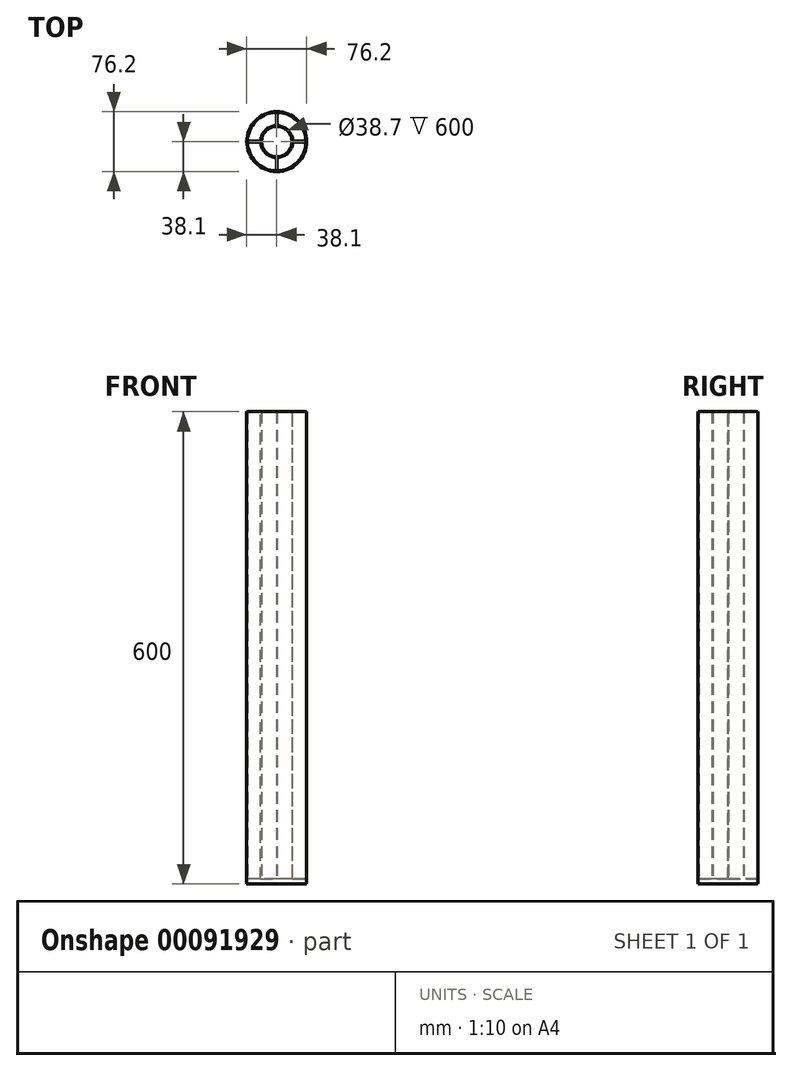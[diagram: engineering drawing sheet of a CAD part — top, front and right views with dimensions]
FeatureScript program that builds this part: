
annotation { "Feature Type Name" : "Feature", "Feature Type Description" : "" }
export const myFeature = defineFeature(function(context is Context, id is Id, definition is map)
    precondition{}
    {
        {
            var Q0;
            Q0=qCreatedBy(makeId("Top.planeOp"),FACE);
            var sketch = newSketch(context, id + "F0", { "sketchPlane" : qUnion([Q0])});
            skCircle(sketch, "E0", {"center": v(0, 0) * mm, "radius": 19.35 * mm});
            skCircle(sketch, "E1", {"center": v(0, 0) * mm, "radius": 38.1 * mm});
            skCircle(sketch, "E2.0", {"center": v(0, 0) * mm, "radius": 37.1 * mm});
            skCircle(sketch, "E3.0", {"center": v(0, 0) * mm, "radius": 20.35 * mm});
            skLineSegment(sketch, "E4.left", {"start": v(-20.35, 0) * mm, "end": v(-20.35, 0) * mm});
            skLineSegment(sketch, "E4.right", {"start": v(-37.1, 0) * mm, "end": v(-37.1, 0) * mm});
            skLineSegment(sketch, "E5.0", {"start": v(-20.35, 0.5) * mm, "end": v(-37, 0.5) * mm});
            skLineSegment(sketch, "E6.0", {"start": v(-20.35, -0.5) * mm, "end": v(-37, -0.5) * mm});
            skLineSegment(sketch, "E7.0", {"start": v(-0.5, 37.27) * mm, "end": v(-0.5, 20.35) * mm});
            skLineSegment(sketch, "E8.0", {"start": v(0.5, 37.27) * mm, "end": v(0.5, 20.35) * mm});
            skLineSegment(sketch, "E9.0", {"start": v(20.35, -0.5) * mm, "end": v(37.64, -0.5) * mm});
            skLineSegment(sketch, "E10.0", {"start": v(20.35, 0.5) * mm, "end": v(37.64, 0.5) * mm});
            skLineSegment(sketch, "E11", {"start": v(20.35, 0.5) * mm, "end": v(20.35, -0.5) * mm});
            skLineSegment(sketch, "E12", {"start": v(37.64, -0.5) * mm, "end": v(37.64, 0.5) * mm});
            skLineSegment(sketch, "E13", {"start": v(-0.5, 20.35) * mm, "end": v(0.5, 20.35) * mm});
            skLineSegment(sketch, "E14", {"start": v(-0.5, 37.27) * mm, "end": v(0.5, 37.27) * mm});
            skLineSegment(sketch, "E15", {"start": v(-37, 0.5) * mm, "end": v(-37, -0.5) * mm});
            skLineSegment(sketch, "E16", {"start": v(-20.35, 0.5) * mm, "end": v(-20.35, -0.5) * mm});
            skLineSegment(sketch, "E17.0", {"start": v(-0.5, -20.35) * mm, "end": v(-0.5, -37.2) * mm});
            skLineSegment(sketch, "E18.0", {"start": v(0.5, -20.35) * mm, "end": v(0.5, -37.2) * mm});
            skLineSegment(sketch, "E19", {"start": v(-0.5, -37.2) * mm, "end": v(0.5, -37.2) * mm});
            skLineSegment(sketch, "E20", {"start": v(0.5, -20.35) * mm, "end": v(-0.5, -20.35) * mm});
            skSolve(sketch);
        }
        {
            var Q0;
            {var subQ3=sQuery(id+"F0.wireOp",EDGE,"E2.0");var subQ5=sQuery(id+"F0.wireOp",EDGE,"E10.0");var subQ6=makeQuery(id+"F0.imprint","INTERSECT",VERTEX,{"derivedFrom":[subQ3,subQ5]});Q0=makeQuery(id+"F0.imprint","IMPRINT",FACE,{"disambiguationData":[TD([[makeQuery(id+"F0.imprint","IMPRINT",EDGE,{"disambiguationData":[TD([[subQ6,1.0]])],"derivedFrom":subQ3}),1.0]])]});}
            var Q1;
            {var subQ5=sQuery(id+"F0.wireOp",EDGE,"E12");Q1=makeQuery(id+"F0.imprint","IMPRINT",FACE,{"disambiguationData":[TD([[makeQuery(id+"F0.imprint","IMPRINT",EDGE,{"derivedFrom":subQ5}),1.0]])]});}
            var Q2;
            Q2=makeQuery(id+"F0.imprint","IMPRINT",FACE,{"disambiguationData":[TD([[makeQuery(id+"F0.imprint","IMPRINT",EDGE,{"derivedFrom":sQuery(id+"F0.wireOp",EDGE,"E1")}),1.0]])]});
            var Q3;
            Q3=makeQuery(id+"F0.imprint","IMPRINT",FACE,{"disambiguationData":[TD([[makeQuery(id+"F0.imprint","IMPRINT",EDGE,{"derivedFrom":sQuery(id+"F0.wireOp",EDGE,"E0")}),-1.0]])]});
            var Q4;
            {var subQ3=sQuery(id+"F0.wireOp",EDGE,"E2.0");var subQ5=sQuery(id+"F0.wireOp",EDGE,"E17.0");var subQ7=makeQuery(id+"F0.imprint","INTERSECT",VERTEX,{"derivedFrom":[subQ3,subQ5]});Q4=makeQuery(id+"F0.imprint","IMPRINT",FACE,{"disambiguationData":[TD([[makeQuery(id+"F0.imprint","IMPRINT",EDGE,{"disambiguationData":[TD([[subQ7,-1.0]])],"derivedFrom":subQ3}),1.0]])]});}
            var Q5;
            {var subQ5=sQuery(id+"F0.wireOp",EDGE,"E19");Q5=makeQuery(id+"F0.imprint","IMPRINT",FACE,{"disambiguationData":[TD([[makeQuery(id+"F0.imprint","IMPRINT",EDGE,{"derivedFrom":subQ5}),1.0]])]});}
            var Q6;
            {var subQ1=sQuery(id+"F0.wireOp",EDGE,"E5.0");Q6=makeQuery(id+"F0.imprint","IMPRINT",FACE,{"disambiguationData":[TD([[makeQuery(id+"F0.imprint","IMPRINT",EDGE,{"derivedFrom":subQ1}),1.0]])]});}
            var Q7;
            {var subQ5=sQuery(id+"F0.wireOp",EDGE,"E14");Q7=makeQuery(id+"F0.imprint","IMPRINT",FACE,{"disambiguationData":[TD([[makeQuery(id+"F0.imprint","IMPRINT",EDGE,{"derivedFrom":subQ5}),-1.0]])]});}
            var Q8;
            {var subQ4=sQuery(id+"F0.wireOp",EDGE,"E2.0");var subQ6=sQuery(id+"F0.wireOp",EDGE,"E8.0");var subQ8=makeQuery(id+"F0.imprint","INTERSECT",VERTEX,{"derivedFrom":[subQ4,subQ6]});Q8=makeQuery(id+"F0.imprint","IMPRINT",FACE,{"disambiguationData":[TD([[makeQuery(id+"F0.imprint","IMPRINT",EDGE,{"disambiguationData":[TD([[subQ8,-1.0]])],"derivedFrom":subQ4}),1.0]])]});}
            extrude(context, id + "F1", {"entities" : qUnion([Q0, Q1, Q2, Q3, Q4, Q5, Q6, Q7, Q8]), "depth" : 600 * mm});
        }
        {
            var Q0;
            Q0=qCreatedBy(makeId("Top.planeOp"),FACE);
            var sketch = newSketch(context, id + "F2", { "sketchPlane" : qUnion([Q0])});
            skCircle(sketch, "E21", {"center": v(0, 0) * mm, "radius": 19.35 * mm});
            skCircle(sketch, "E22", {"center": v(0, 0) * mm, "radius": 38.1 * mm});
            skSolve(sketch);
        }
        {
            var Q0;
            Q0 = qSketchRegion(id + "F2", true);
            extrude(context, id + "F3", {"entities" : qUnion([Q0]), "operationType" : NewBodyOperationType.ADD, "depth" : 6.35 * mm});
        }
    });
